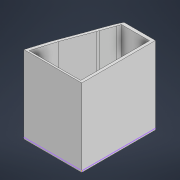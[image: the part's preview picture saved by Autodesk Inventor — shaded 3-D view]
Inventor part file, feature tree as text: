
AUTODESK INVENTOR PART (.ipt)
format: ipt  version: 2022 (Build 260153000, 153)  size: 110,080 bytes
history: native  units: mm
features: extrude x2, sketch x1
ambient origin geometry x8: Origin, YZ Plane, XZ Plane, XY Plane, X Axis, Y Axis, Z Axis, Center Point
bodies: Solid1 (feature_tree)
feature tree (3):
  sketch  "Sketch1"  dims[d1=2.5mm d2=0.0mm d3=111.5mm d4=0.0mm d5=0.5mm d6=0.872665mm]
  extrude  "Extrusion1"  Depth=111.5mm TaperAngle=0.0deg
  extrude  "Extrusion2"  Depth=111.5mm
